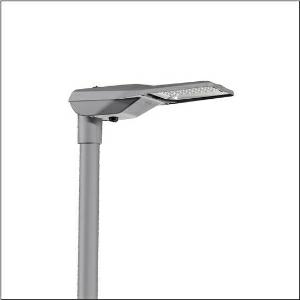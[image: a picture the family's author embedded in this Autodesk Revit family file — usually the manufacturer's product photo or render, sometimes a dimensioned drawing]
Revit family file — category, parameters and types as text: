
# Revit family: streetlight_sl_21_iq_mini___st0_8a_5xe2c31y08jb_7a77
name_source: partatom
category: Lighting Fixtures
units: mm (PartAtom-declared; Revit-internal decimal feet)

## family parameters
Cut with Voids When Loaded = No
Host = Face
Light Source = No
Part Type = Normal
Room Calculation Point = No
Round Connector Dimension = Use Diameter
Shared = No

## types (1)
- --- (1 x LED, 11210 lm, 72.5 W, 3000K)
    Apparent Load = 73 VA
    CIE Flux Codes = 41 75 97 100 100
    Color Rendering = 70
    Color Temperature = 3000K
    Default Elevation = 1800 mm
    Description = Streetlight SL 21 iQ mini, mast luminaire, primary light control with lens, of PMMA, primary optical cover: cover, of toughened safety glass, transparent, light distribution: ST0.8a, light emission: direct distribution, primary light characteristic: asymmetric, installation type: post-top, side-entry, LED, High Power LED, rated luminous flux: 11.210lm, luminous efficacy: 155lm/W, light colour: 730, colour temperature: 3000K, control gear: iQ-Street Remote, D4i with power reduction, control: pre-setting: logarithmic dimming characteristic, Street-Remote, Auto-Match, Temp-Guard, Lumen-Switch, Night-Set, Smart-Wire, Light-Fading, Desk-Remote (wireless, voltage-free reading and setting of iQ features in the workshop via application-optimized NFC function/RFID function), optimised constant luminous flux control (CLO 2.0), mains connection: 220..240V, AC, 50/60Hz, start of lifetime: 73W, end of service life: 76W, reduction: 33W, luminaire housing, of diecast aluminium, powder-coated, Siteco® metallic grey (DB 702S), corrosivity category C5 mid according to DIN EN ISO 12944, please order mast flange separately, inclination adjustable: 0°, 5°, 10°, 15°, sealing non-destructively replaceable, multi-level sealing system, length: 628mm, width: 235mm, height: 110mm, mast flange for spigot size: 42mm (side-entry): 5XC10008XM4, 60/48mm (side-entry/post-top): 5XC10108XM2, 76/60mm (side-entry/post-top): 5XC10108XM1, mounting height: 4..8m, Smart Interface below and above, protection rating (complete): IP66, insulation class (complete): insulation class II (safety insulation), certification: CE, ENEC, ENEC+, VDE, impact resistance: IK10, permissible operating ambient temperature for outdoor applications: -40..+50°C, standard-compliant lighting for roads and squares, packaging unit: 1 piece

Light Distribution: ST0.8a
    Height = 110 mm
    Lamp = 1 x LED
    Lamp Light Flux = 11210 lm
    Lamp Power = 72.5 W
    Lamp count = 1
    Length = 625 mm
    Luminous efficacy = 155 lm/W
    Manufacturer = Siteco
    ModVariant = No
    Model = 5XE2C31Y08JB
    Number of Poles = 1
    OnlyDefault = Yes
    Power Factor = 1
    Product Name = Streetlight SL 21 iQ mini | ST0.8a
    Product group = mast luminaire | pylon top
    ProductGroupID = 6100
    Protection Class = Protection class II
    Protection Degree = IP 66
    RLX_Detail_Level = 1
    RLX_Emergency_Light_Flux = 0 lm
    RLX_Emergency_Type = 0
    RLX_Emergency_Type_DB = No
    RlxData = <blob elided: 26705 chars, md5=b949dfb9>
    Socket = socket
    Standby Power = 0 W
    System Light Flux = 11210 lm
    System Power = 73 W
    Type Comments = factory setting: luminous flux: 100 % | dim-lin: 254 | 755 mA
    Type Image = l_1003514.jpg
    URL = http://relux.com
    VarID = @adj_113232
    Voltage = 0 V
    Weight = 0.00 kg
    Width = 234 mm

## geometry (parser evidence)
native form markers: Blend x4, Sweep x13
no freeform markers — native parametric forms only
